# Revit family: Vitra-FilteredStopTap-OtherSeries-A45200
name_source: partatom
category: Plumbing Fixtures
revit_build: Autodesk Revit 2017 (Build: 20160225_1515(x64)
units: mm (PartAtom-declared; Revit-internal decimal feet)

## family parameters
Cut with Voids When Loaded = No
Host = Face
OmniClass Number = 23.45.00.00
OmniClass Title = Sanitary, Laundry, and Cleaning Equipment
Part Type = Normal
Room Calculation Point = No
Round Connector Dimension = Use Diameter
Shared = Yes

## types (1)
- AngleStopValve-Vitra-OtherSeries-A45200
    Article No. (default) = A45200
    BIMobject category = Taps & Mixers
    CW Connection = Yes
    Coating Material = Vitra-Chrome
    Color = Chrome
    Connection Diameter (mm) = 15 mm  [stored 0.0492126 ft]
    Cost = 0 $
    Default Elevation = 850 mm  [stored 2.78871 ft]
    Depth(mm) = 65 mm  [stored 0.213255 ft]
    Design country = Turkey
    HW Connection = Yes
    Height(mm) = 50 mm
    Hot Water Supply (max.) = 80 °C
    Hot Water temperature, factory set to = 38 °C
    IFC Classification = Sanitary Terminal
    Main Material = Brass
    Manufacturer = Vitra
    Manufacturer name = Vitra
    Masterformat 2014 Code = 22 40 00
    Masterformat 2014 Description = Plumbing Fixtures
    Min. flow pressure of = 0.5 bar
    Model = A45200
    MountingType = Pipe Connect
    NBS Referans Code = 45-35-70/371
    NBS Referans Description = Water supply fittings for wash basins and troughs
    Nominal height = 0.000
    Nominal width = 0.000
    Number Of Connections = 1 mm  [stored 0.00328084 ft]
    OmniClass Code = 23-31 11 19 11
    OmniClass Description = Thermostatically Controlled Faucet Mixing Valves
    Product SKU = A45200
    Product Type = Angle Stop Valve
    Product certification = https://vitraglobal.com
    Product data url = https://www.vitra.com.tr
    Product family = Other Series
    Product group = Angle Stop Valve
    Range of Hot Water Supply = 5 - 65 °C
    Range of flow pressure = 1 - 5 bar
    Technical description = https://www.vitra.com.tr
    Test Pressure = 16 bar
    UNSPSC Code = 40141616
    UNSPSC Description = Valve parts or accessories
    URL = https://vitraglobal.com
    Uniclass 1.4 Code = L7117
    Uniclass 1.4 Description = Valves for water supply/distribution
    Uniclass 2.0 Code = Pr_94
    Uniclass 2.0 Description = Valves
    Uniclass 2015 Code = Pr_65_54
    Uniclass 2015 Name = Valve products
    Warranty Period (Year) = 10 Years
    Weight Net (kg) = 0,142
    Width(mm) = 65 mm  [stored 0.213255 ft]
    Youtube = https://www.youtube.com

note: [stored X ft] marks values corroborated as IEEE doubles in the binary element streams (Revit-internal decimal feet)

## geometry (parser evidence)
native form markers: Sweep x3
no freeform markers — native parametric forms only
